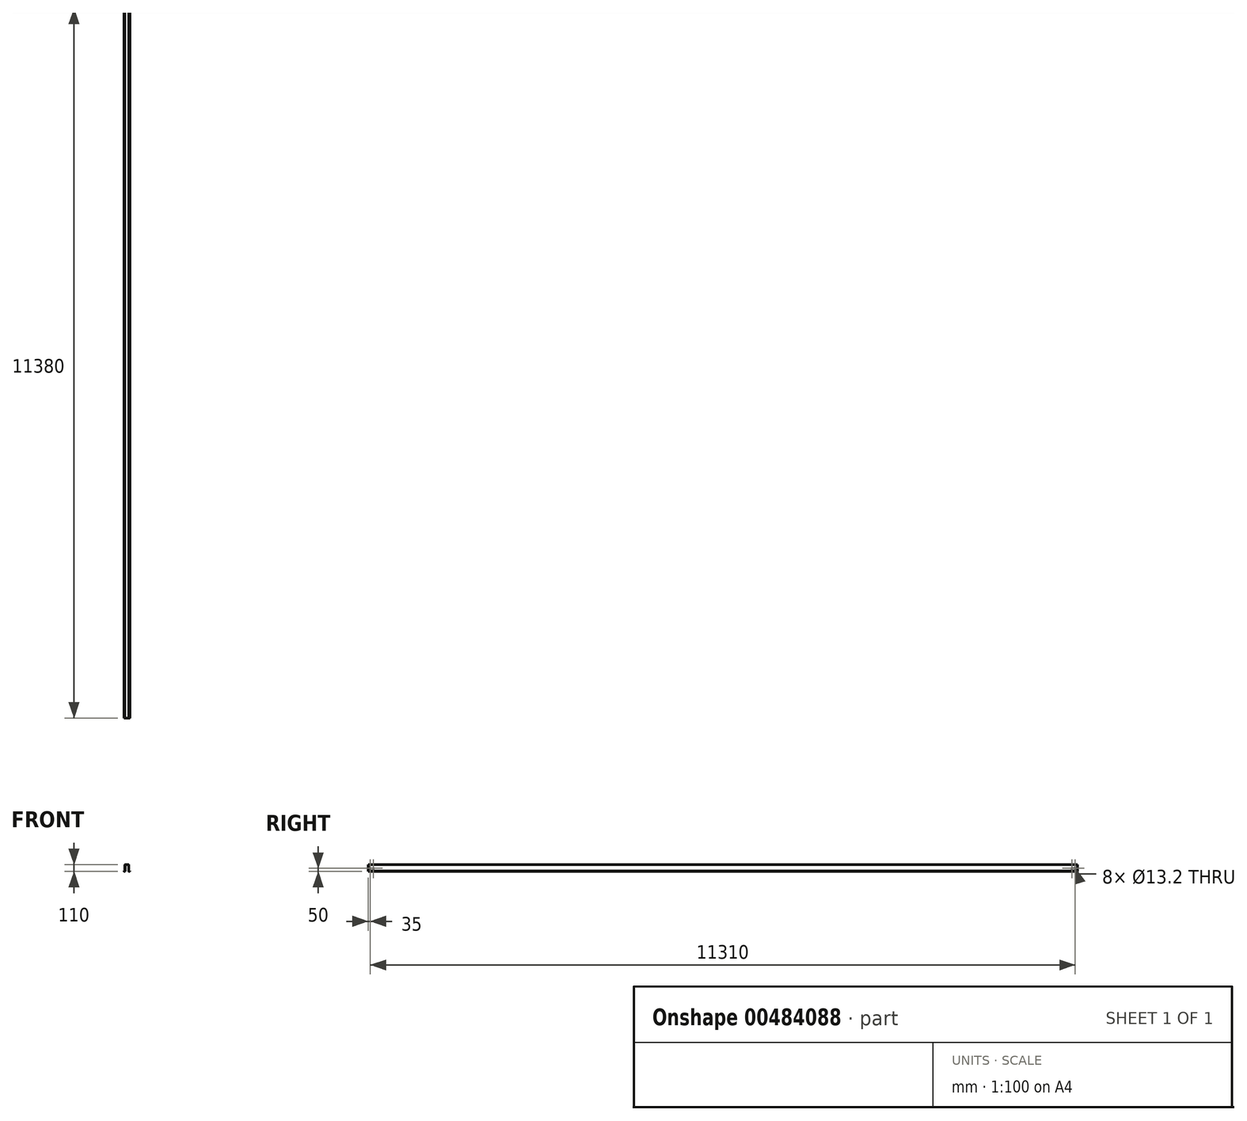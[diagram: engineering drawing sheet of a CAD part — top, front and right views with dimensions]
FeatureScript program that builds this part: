
annotation { "Feature Type Name" : "Feature", "Feature Type Description" : "" }
export const myFeature = defineFeature(function(context is Context, id is Id, definition is map)
    precondition{}
    {
        {
            var Q0;
            Q0=qCreatedBy(makeId("Front.planeOp"),FACE);
            var sketch = newSketch(context, id + "F0", { "sketchPlane" : qUnion([Q0])});
            skLineSegment(sketch, "E0", {"start": v(0, 0) * mm, "end": v(0, -3) * mm});
            skLineSegment(sketch, "E1", {"start": v(5, -8) * mm, "end": v(11, -8) * mm});
            skLineSegment(sketch, "E2", {"start": v(16, -3) * mm, "end": v(16, 95) * mm});
            skLineSegment(sketch, "E3", {"start": v(21, 100) * mm, "end": v(71, 100) * mm});
            skLineSegment(sketch, "E4", {"start": v(76, 95) * mm, "end": v(76, -3) * mm});
            skLineSegment(sketch, "E5", {"start": v(81, -8) * mm, "end": v(87, -8) * mm});
            skLineSegment(sketch, "E6", {"start": v(92, -3) * mm, "end": v(92, 0) * mm});
            skLineSegment(sketch, "E7", {"start": v(92, 0) * mm, "end": v(94, 0) * mm});
            skLineSegment(sketch, "E8", {"start": v(94, 0) * mm, "end": v(94, -5) * mm});
            skLineSegment(sketch, "E9", {"start": v(89, -10) * mm, "end": v(79, -10) * mm});
            skLineSegment(sketch, "E10", {"start": v(74, -5) * mm, "end": v(74, 93) * mm});
            skLineSegment(sketch, "E11", {"start": v(69, 98) * mm, "end": v(23, 98) * mm});
            skLineSegment(sketch, "E12", {"start": v(18, 93) * mm, "end": v(18, -5) * mm});
            skLineSegment(sketch, "E13", {"start": v(13, -10) * mm, "end": v(3, -10) * mm});
            skLineSegment(sketch, "E14", {"start": v(-2, -5) * mm, "end": v(-2, 0) * mm});
            skLineSegment(sketch, "E15", {"start": v(-2, 0) * mm, "end": v(0, 0) * mm});
            skPoint(sketch, "E16.visualSharp", {"position": v(18, 98) * mm});
            skArc(sketch, "E16.filletArc", {"start": v(23, 98) * mm, "mid": v(19.46, 96.54) * mm, "end": v(18, 93) * mm});
            skPoint(sketch, "E17.visualSharp", {"position": v(74, 98) * mm});
            skArc(sketch, "E17.filletArc", {"start": v(74, 93) * mm, "mid": v(72.54, 96.54) * mm, "end": v(69, 98) * mm});
            skPoint(sketch, "E18.visualSharp", {"position": v(16, 100) * mm});
            skArc(sketch, "E18.filletArc", {"start": v(21, 100) * mm, "mid": v(17.46, 98.54) * mm, "end": v(16, 95) * mm});
            skPoint(sketch, "E19.visualSharp", {"position": v(76, 100) * mm});
            skArc(sketch, "E19.filletArc", {"start": v(76, 95) * mm, "mid": v(74.54, 98.54) * mm, "end": v(71, 100) * mm});
            skPoint(sketch, "E20.visualSharp", {"position": v(74, -10) * mm});
            skArc(sketch, "E20.filletArc", {"start": v(74, -5) * mm, "mid": v(75.46, -8.54) * mm, "end": v(79, -10) * mm});
            skPoint(sketch, "E21.visualSharp", {"position": v(76, -8) * mm});
            skArc(sketch, "E21.filletArc", {"start": v(76, -3) * mm, "mid": v(77.46, -6.54) * mm, "end": v(81, -8) * mm});
            skPoint(sketch, "E22.visualSharp", {"position": v(92, -8) * mm});
            skArc(sketch, "E22.filletArc", {"start": v(87, -8) * mm, "mid": v(90.54, -6.54) * mm, "end": v(92, -3) * mm});
            skPoint(sketch, "E23.visualSharp", {"position": v(94, -10) * mm});
            skArc(sketch, "E23.filletArc", {"start": v(89, -10) * mm, "mid": v(92.54, -8.54) * mm, "end": v(94, -5) * mm});
            skPoint(sketch, "E24.visualSharp", {"position": v(18, -10) * mm});
            skArc(sketch, "E24.filletArc", {"start": v(13, -10) * mm, "mid": v(16.54, -8.54) * mm, "end": v(18, -5) * mm});
            skPoint(sketch, "E25.visualSharp", {"position": v(16, -8) * mm});
            skArc(sketch, "E25.filletArc", {"start": v(11, -8) * mm, "mid": v(14.54, -6.54) * mm, "end": v(16, -3) * mm});
            skPoint(sketch, "E26.visualSharp", {"position": v(-2, -10) * mm});
            skArc(sketch, "E26.filletArc", {"start": v(-2, -5) * mm, "mid": v(-0.54, -8.54) * mm, "end": v(3, -10) * mm});
            skPoint(sketch, "E27.visualSharp", {"position": v(0, -8) * mm});
            skArc(sketch, "E27.filletArc", {"start": v(0, -3) * mm, "mid": v(1.46, -6.54) * mm, "end": v(5, -8) * mm});
            skSolve(sketch);
        }
        {
            var Q0;
            Q0=qSketchRegion(id+"F0",true);
            extrude(context, id + "F1", {"entities" : qUnion([Q0]), "depth" : 11380 * mm, "offsetDistance" : 25 * mm});
        }
        {
            var Q0;
            Q0=makeQuery(id+"F1.opExtrude","SWEPT_FACE",FACE,{"disambiguationData":[OSD([sQuery(id+"F0.wireOp",EDGE,"E4")])]});
            var sketch = newSketch(context, id + "F2", { "sketchPlane" : qUnion([Q0])});
            skLineSegment(sketch, "E28", {"start": v(0, 46) * mm, "end": v(-35, 46) * mm});
            skLineSegment(sketch, "E29", {"start": v(-35, 46) * mm, "end": v(-85, 46) * mm});
            skLineSegment(sketch, "E30", {"start": v(-11380, 46) * mm, "end": v(-11345, 46) * mm});
            skLineSegment(sketch, "E31", {"start": v(-11345, 46) * mm, "end": v(-11295, 46) * mm});
            skLineSegment(sketch, "E32", {"start": v(-85, 46) * mm, "end": v(-85, 40) * mm});
            skLineSegment(sketch, "E33", {"start": v(-35, 46) * mm, "end": v(-35, 40) * mm});
            skLineSegment(sketch, "E34", {"start": v(-11345, 46) * mm, "end": v(-11345, 40) * mm});
            skLineSegment(sketch, "E35", {"start": v(-11295, 46) * mm, "end": v(-11295, 40) * mm});
            skSolve(sketch);
        }
        {
            var Q0;
            Q0=sQuery(id+"F2.wireOp",VERTEX,"E34.end");
            var Q1;
            Q1=sQuery(id+"F2.wireOp",VERTEX,"E35.end");
            var Q2;
            Q2=sQuery(id+"F2.wireOp",VERTEX,"E32.end");
            var Q3;
            Q3=sQuery(id+"F2.wireOp",VERTEX,"E33.end");
            var Q4;
            Q4=makeQuery(id+"F1.opExtrude","SWEPT_BODY",BODY,{"disambiguationData":[OSD([sQuery(id+"F0.wireOp",EDGE,"E0"),sQuery(id+"F0.wireOp",EDGE,"E1"),sQuery(id+"F0.wireOp",EDGE,"E2"),sQuery(id+"F0.wireOp",EDGE,"E3"),sQuery(id+"F0.wireOp",EDGE,"E4"),sQuery(id+"F0.wireOp",EDGE,"E5"),sQuery(id+"F0.wireOp",EDGE,"E6"),sQuery(id+"F0.wireOp",EDGE,"E7"),sQuery(id+"F0.wireOp",EDGE,"E8"),sQuery(id+"F0.wireOp",EDGE,"E9"),sQuery(id+"F0.wireOp",EDGE,"E10"),sQuery(id+"F0.wireOp",EDGE,"E11"),sQuery(id+"F0.wireOp",EDGE,"E12"),sQuery(id+"F0.wireOp",EDGE,"E13"),sQuery(id+"F0.wireOp",EDGE,"E14"),sQuery(id+"F0.wireOp",EDGE,"E15"),sQuery(id+"F0.wireOp",EDGE,"E16.filletArc"),sQuery(id+"F0.wireOp",EDGE,"E17.filletArc"),sQuery(id+"F0.wireOp",EDGE,"E18.filletArc"),sQuery(id+"F0.wireOp",EDGE,"E19.filletArc"),sQuery(id+"F0.wireOp",EDGE,"E20.filletArc"),sQuery(id+"F0.wireOp",EDGE,"E21.filletArc"),sQuery(id+"F0.wireOp",EDGE,"E22.filletArc"),sQuery(id+"F0.wireOp",EDGE,"E23.filletArc"),sQuery(id+"F0.wireOp",EDGE,"E24.filletArc"),sQuery(id+"F0.wireOp",EDGE,"E25.filletArc"),sQuery(id+"F0.wireOp",EDGE,"E26.filletArc"),sQuery(id+"F0.wireOp",EDGE,"E27.filletArc")])]});
            hole(context, id + "F3", {"style" : HoleStyle.SIMPLE, "endStyle" : HoleEndStyle.THROUGH, "standardTappedOrClearance" : lookupTablePath({ "standard" : "ISO", "fit" : "Normal", "size" : "M12", "type" : "Clearance" }), "standardBlindInLast" : lookupTablePath({ "fit" : "Standard", "standard" : "ISO", "size" : "M12", "type" : "Clearance" }), "holeDiameter" : 13.2 * mm, "isTappedThrough" : true, "tappedDepth" : 12 * mm, "tapClearance" : 3, "locations" : qUnion([Q0, Q1, Q2, Q3]), "scope" : qUnion([Q4])});
        }
    });
